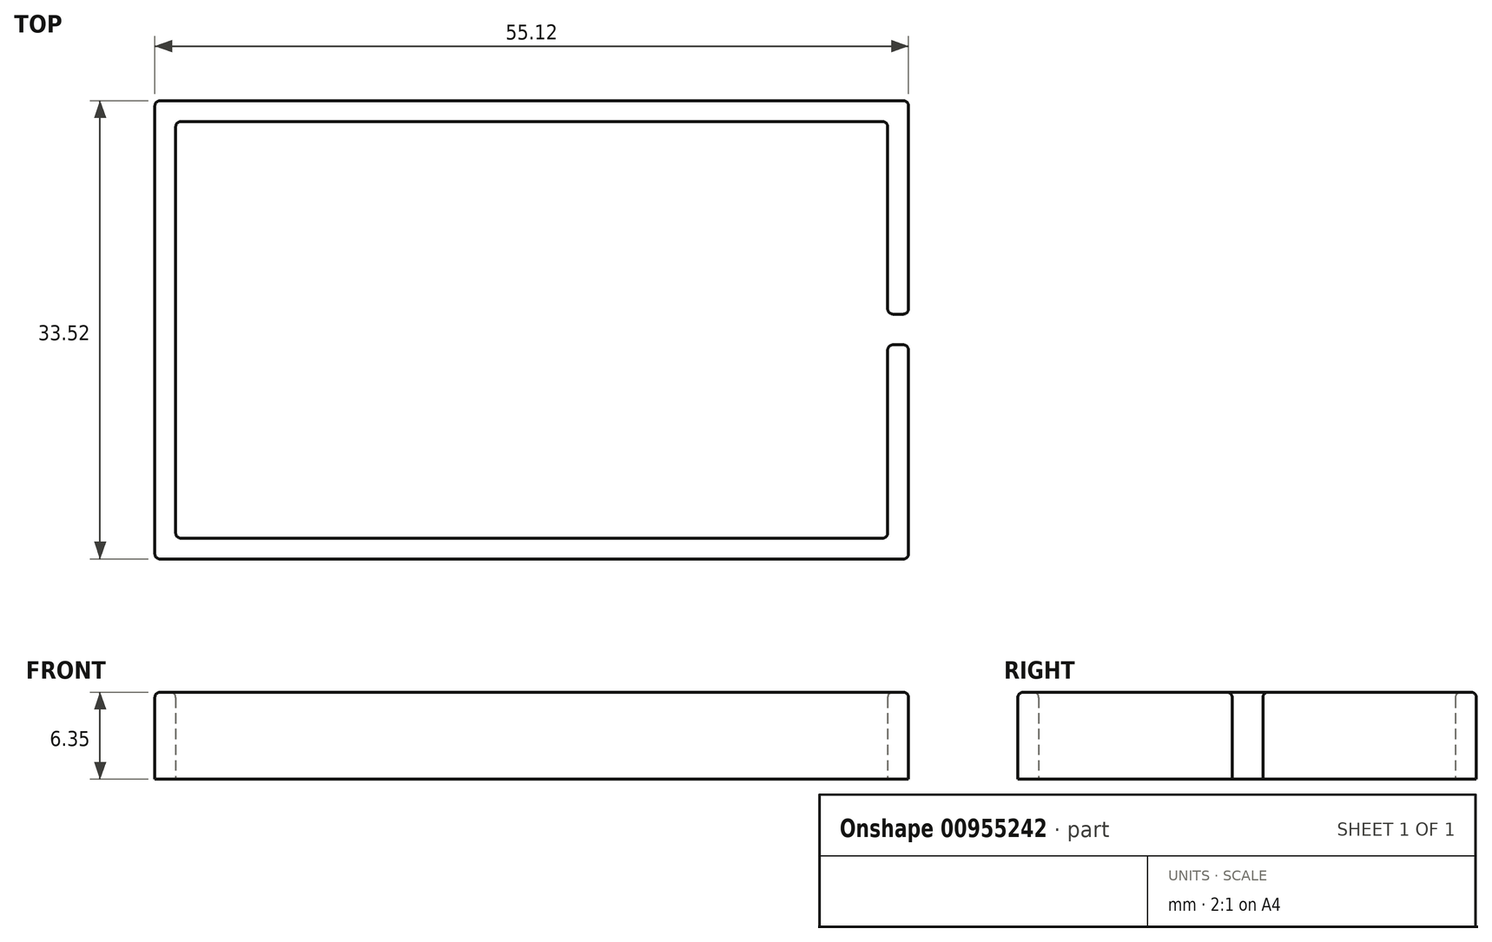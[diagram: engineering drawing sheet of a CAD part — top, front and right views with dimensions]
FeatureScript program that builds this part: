
annotation { "Feature Type Name" : "Feature", "Feature Type Description" : "" }
export const myFeature = defineFeature(function(context is Context, id is Id, definition is map)
    precondition{}
    {
        {
            var Q0;
            Q0=qCreatedBy(makeId("Top.planeOp"),FACE);
            var sketch = newSketch(context, id + "F0", { "sketchPlane" : qUnion([Q0])});
            skLineSegment(sketch, "E0.bottom", {"start": v(-26.03, 15.24) * mm, "end": v(26.04, 15.24) * mm});
            skLineSegment(sketch, "E0.top", {"start": v(-26.04, -15.24) * mm, "end": v(26.03, -15.24) * mm});
            skLineSegment(sketch, "E0.left", {"start": v(-26.03, 15.24) * mm, "end": v(-26.04, -15.24) * mm});
            skLineSegment(sketch, "E0.right", {"start": v(26.04, 15.24) * mm, "end": v(26.03, -15.24) * mm});
            skPoint(sketch, "E0.middle", {"position": v(0, 0) * mm});
            skLineSegment(sketch, "E1.bottom", {"start": v(-27.56, 16.76) * mm, "end": v(27.56, 16.76) * mm});
            skLineSegment(sketch, "E1.top", {"start": v(-27.56, -16.76) * mm, "end": v(27.56, -16.76) * mm});
            skLineSegment(sketch, "E1.left", {"start": v(-27.56, 16.76) * mm, "end": v(-27.56, -16.76) * mm});
            skLineSegment(sketch, "E1.right", {"start": v(27.56, 16.76) * mm, "end": v(27.56, -16.76) * mm});
            skLineSegment(sketch, "E2.bottom", {"start": v(24.64, 0) * mm, "end": v(30.94, 0) * mm});
            skLineSegment(sketch, "E2.top", {"start": v(24.64, -1.1) * mm, "end": v(30.94, -1.1) * mm});
            skLineSegment(sketch, "E2.left", {"start": v(24.64, 0) * mm, "end": v(24.64, -1.1) * mm});
            skLineSegment(sketch, "E2.right", {"start": v(30.94, 0) * mm, "end": v(30.94, -1.1) * mm});
            skLineSegment(sketch, "E3.bottom", {"start": v(24.64, 0) * mm, "end": v(30.92, 0) * mm});
            skLineSegment(sketch, "E3.top", {"start": v(24.64, 1.16) * mm, "end": v(30.92, 1.16) * mm});
            skLineSegment(sketch, "E3.left", {"start": v(24.64, 0) * mm, "end": v(24.64, 1.16) * mm});
            skLineSegment(sketch, "E3.right", {"start": v(30.92, 0) * mm, "end": v(30.92, 1.16) * mm});
            skSolve(sketch);
        }
        {
            var Q0;
            Q0=makeQuery(id+"F0.imprint","IMPRINT",FACE,{"disambiguationData":[TD([[makeQuery(id+"F0.imprint","IMPRINT",EDGE,{"derivedFrom":sQuery(id+"F0.wireOp",EDGE,"E0.bottom")}),1.0]])]});
            extrude(context, id + "F1", {"entities" : qUnion([Q0]), "depth" : 6.35 * mm, "offsetDistance" : 25.4 * mm});
        }
        {
            var Q0;
            Q0=makeQuery(id+"F1.opExtrude","CAP_FACE",FACE,{"disambiguationData":[OSD([sQuery(id+"F0.wireOp",EDGE,"E0.bottom"),sQuery(id+"F0.wireOp",EDGE,"E0.top"),sQuery(id+"F0.wireOp",EDGE,"E0.left"),sQuery(id+"F0.wireOp",EDGE,"E0.right"),sQuery(id+"F0.wireOp",EDGE,"E1.bottom"),sQuery(id+"F0.wireOp",EDGE,"E1.top"),sQuery(id+"F0.wireOp",EDGE,"E1.left"),sQuery(id+"F0.wireOp",EDGE,"E1.right"),sQuery(id+"F0.wireOp",EDGE,"E2.top"),sQuery(id+"F0.wireOp",EDGE,"E3.top")])],"isStart":false});
            var Q1;
            Q1=makeQuery(id+"F1.opExtrude","SWEPT_EDGE",EDGE,{"disambiguationData":[OSD([sQuery(id+"F0.wireOp",EDGE,"E1.top"),sQuery(id+"F0.wireOp",EDGE,"E1.right")])]});
            var Q2;
            Q2=makeQuery(id+"F1.opExtrude","SWEPT_EDGE",EDGE,{"disambiguationData":[OSD([sQuery(id+"F0.wireOp",EDGE,"E1.top"),sQuery(id+"F0.wireOp",EDGE,"E1.left")])]});
            var Q3;
            Q3=makeQuery(id+"F1.opExtrude","SWEPT_EDGE",EDGE,{"disambiguationData":[OSD([sQuery(id+"F0.wireOp",EDGE,"E1.bottom"),sQuery(id+"F0.wireOp",EDGE,"E1.left")])]});
            var Q4;
            Q4=makeQuery(id+"F1.opExtrude","SWEPT_EDGE",EDGE,{"disambiguationData":[OSD([sQuery(id+"F0.wireOp",EDGE,"E1.bottom"),sQuery(id+"F0.wireOp",EDGE,"E1.right")])]});
            var Q5;
            Q5=makeQuery(id+"F1.opExtrude","SWEPT_EDGE",EDGE,{"disambiguationData":[OSD([sQuery(id+"F0.wireOp",EDGE,"E1.right"),sQuery(id+"F0.wireOp",EDGE,"E2.top")])]});
            var Q6;
            Q6=makeQuery(id+"F1.opExtrude","SWEPT_EDGE",EDGE,{"disambiguationData":[OSD([sQuery(id+"F0.wireOp",EDGE,"E1.right"),sQuery(id+"F0.wireOp",EDGE,"E3.top")])]});
            var Q7;
            Q7=makeQuery(id+"F1.opExtrude","SWEPT_EDGE",EDGE,{"disambiguationData":[OSD([sQuery(id+"F0.wireOp",EDGE,"E0.top"),sQuery(id+"F0.wireOp",EDGE,"E0.left")])]});
            var Q8;
            Q8=makeQuery(id+"F1.opExtrude","SWEPT_EDGE",EDGE,{"disambiguationData":[OSD([sQuery(id+"F0.wireOp",EDGE,"E0.bottom"),sQuery(id+"F0.wireOp",EDGE,"E0.left")])]});
            var Q9;
            Q9=makeQuery(id+"F1.opExtrude","SWEPT_EDGE",EDGE,{"disambiguationData":[OSD([sQuery(id+"F0.wireOp",EDGE,"E0.bottom"),sQuery(id+"F0.wireOp",EDGE,"E0.right")])]});
            var Q10;
            Q10=makeQuery(id+"F1.opExtrude","SWEPT_EDGE",EDGE,{"disambiguationData":[OSD([sQuery(id+"F0.wireOp",EDGE,"E0.right"),sQuery(id+"F0.wireOp",EDGE,"E3.top")])]});
            var Q11;
            Q11=makeQuery(id+"F1.opExtrude","SWEPT_EDGE",EDGE,{"disambiguationData":[OSD([sQuery(id+"F0.wireOp",EDGE,"E0.right"),sQuery(id+"F0.wireOp",EDGE,"E2.top")])]});
            var Q12;
            Q12=makeQuery(id+"F1.opExtrude","SWEPT_EDGE",EDGE,{"disambiguationData":[OSD([sQuery(id+"F0.wireOp",EDGE,"E0.top"),sQuery(id+"F0.wireOp",EDGE,"E0.right")])]});
            fillet(context, id + "F2", {"entities" : qUnion([Q0, Q1, Q2, Q3, Q4, Q5, Q6, Q7, Q8, Q9, Q10, Q11, Q12]), "radius" : 0.38 * mm, "tangentPropagation" : true, "allowEdgeOverflow" : false});
        }
    });
